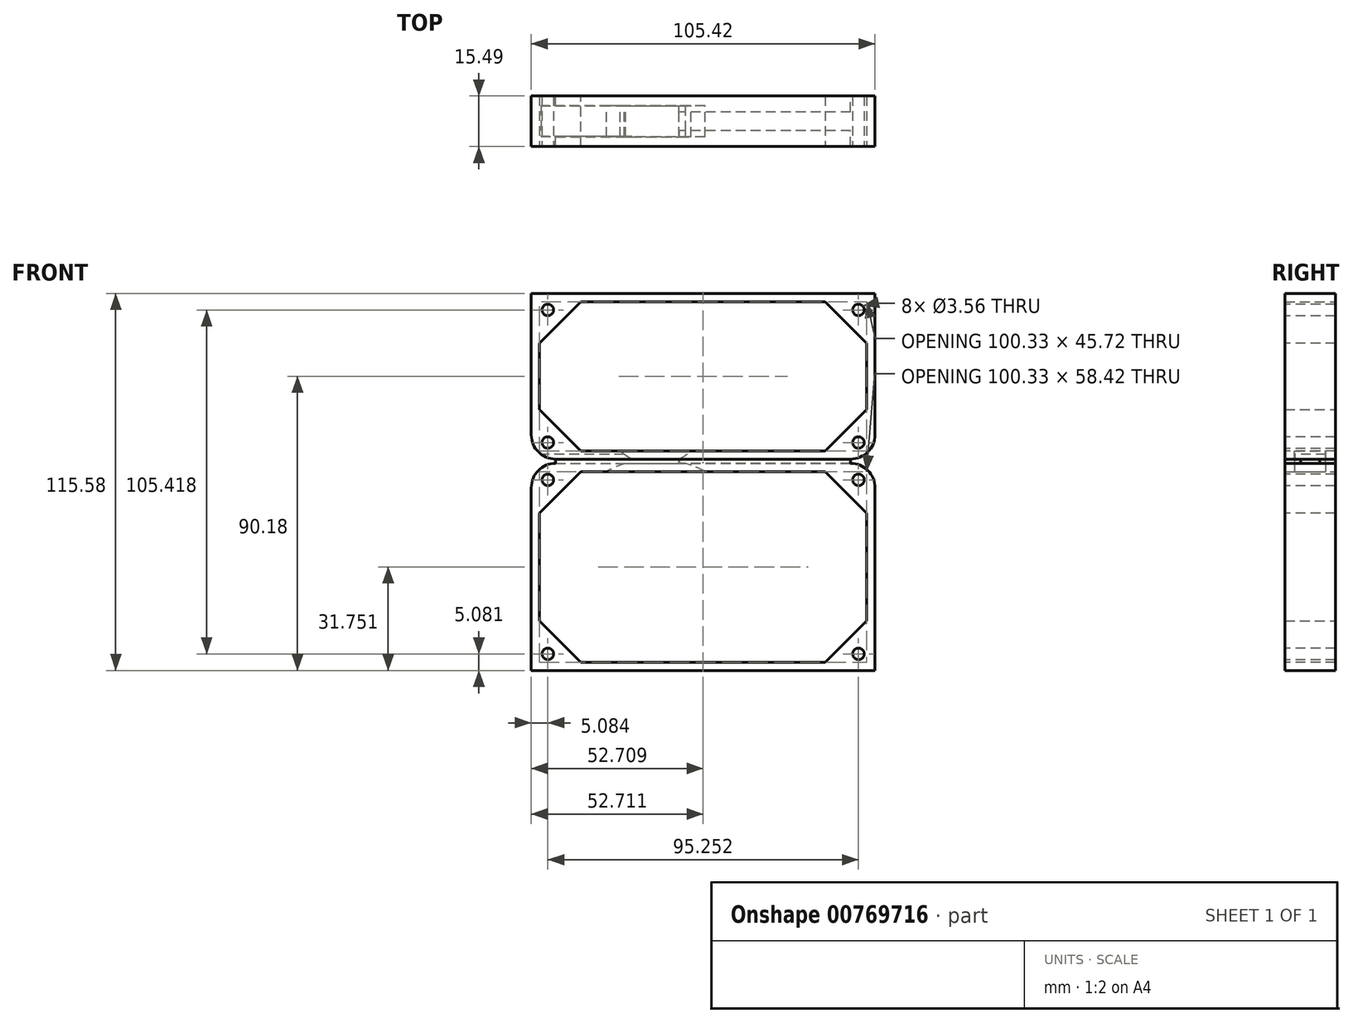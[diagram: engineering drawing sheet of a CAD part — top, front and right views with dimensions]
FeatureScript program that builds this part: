
annotation { "Feature Type Name" : "Feature", "Feature Type Description" : "" }
export const myFeature = defineFeature(function(context is Context, id is Id, definition is map)
    precondition{}
    {
        {
            var Q0;
            Q0=qCreatedBy(makeId("Front.planeOp"),FACE);
            var sketch = newSketch(context, id + "F0", { "sketchPlane" : qUnion([Q0])});
            skLineSegment(sketch, "E0.bottom", {"start": v(-52.7, 0.64) * mm, "end": v(52.7, 0.64) * mm});
            skLineSegment(sketch, "E0.top", {"start": v(-52.7, 51.44) * mm, "end": v(52.7, 51.44) * mm});
            skLineSegment(sketch, "E0.left", {"start": v(-52.7, 0.64) * mm, "end": v(-52.7, 51.44) * mm});
            skLineSegment(sketch, "E0.right", {"start": v(52.7, 0.64) * mm, "end": v(52.7, 51.44) * mm});
            skSolve(sketch);
        }
        {
            var Q0;
            Q0=qCreatedBy(makeId("Front.planeOp"),FACE);
            var sketch = newSketch(context, id + "F1", { "sketchPlane" : qUnion([Q0])});
            skLineSegment(sketch, "E1.bottom", {"start": v(-52.7, -0.64) * mm, "end": v(52.7, -0.64) * mm});
            skLineSegment(sketch, "E1.top", {"start": v(-52.7, -64.14) * mm, "end": v(52.7, -64.14) * mm});
            skLineSegment(sketch, "E1.left", {"start": v(-52.7, -0.64) * mm, "end": v(-52.7, -64.14) * mm});
            skLineSegment(sketch, "E1.right", {"start": v(52.7, -0.64) * mm, "end": v(52.7, -64.14) * mm});
            skSolve(sketch);
        }
        {
            var Q0;
            Q0=makeQuery(id+"F0.imprint","IMPRINT",FACE,{"disambiguationData":[TD([[makeQuery(id+"F0.imprint","IMPRINT",EDGE,{"derivedFrom":sQuery(id+"F0.wireOp",EDGE,"E0.bottom")}),1.0]])]});
            extrude(context, id + "F2", {"entities" : qUnion([Q0]), "depth" : 15.5 * mm, "offsetDistance" : 25.4 * mm});
        }
        {
            var Q0;
            Q0=makeQuery(id+"F1.imprint","IMPRINT",FACE,{"disambiguationData":[TD([[makeQuery(id+"F1.imprint","IMPRINT",EDGE,{"derivedFrom":sQuery(id+"F1.wireOp",EDGE,"E1.bottom")}),-1.0]])]});
            extrude(context, id + "F3", {"entities" : qUnion([Q0]), "depth" : 15.5 * mm, "offsetDistance" : 25.4 * mm});
        }
        {
            var Q0;
            Q0=makeQuery(id+"F2.opExtrude","CAP_FACE",FACE,{"disambiguationData":[OSD([sQuery(id+"F0.wireOp",EDGE,"E0.bottom"),sQuery(id+"F0.wireOp",EDGE,"E0.top"),sQuery(id+"F0.wireOp",EDGE,"E0.left"),sQuery(id+"F0.wireOp",EDGE,"E0.right")])],"isStart":false});
            var sketch = newSketch(context, id + "F4", { "sketchPlane" : qUnion([Q0])});
            skLineSegment(sketch, "E2.bottom", {"start": v(-50.17, 48.9) * mm, "end": v(50.16, 48.9) * mm});
            skLineSegment(sketch, "E2.top", {"start": v(-50.17, 3.18) * mm, "end": v(50.16, 3.18) * mm});
            skLineSegment(sketch, "E2.left", {"start": v(-50.17, 48.9) * mm, "end": v(-50.17, 3.18) * mm});
            skLineSegment(sketch, "E2.right", {"start": v(50.16, 48.9) * mm, "end": v(50.16, 3.18) * mm});
            skSolve(sketch);
        }
        {
            var Q0;
            Q0=makeQuery(id+"F3.opExtrude","CAP_FACE",FACE,{"disambiguationData":[OSD([sQuery(id+"F1.wireOp",EDGE,"E1.bottom"),sQuery(id+"F1.wireOp",EDGE,"E1.top"),sQuery(id+"F1.wireOp",EDGE,"E1.left"),sQuery(id+"F1.wireOp",EDGE,"E1.right")])],"isStart":false});
            var sketch = newSketch(context, id + "F5", { "sketchPlane" : qUnion([Q0])});
            skLineSegment(sketch, "E3.bottom", {"start": v(-50.16, -3.18) * mm, "end": v(50.17, -3.18) * mm});
            skLineSegment(sketch, "E3.top", {"start": v(-50.16, -61.6) * mm, "end": v(50.17, -61.6) * mm});
            skLineSegment(sketch, "E3.left", {"start": v(-50.16, -3.18) * mm, "end": v(-50.16, -61.6) * mm});
            skLineSegment(sketch, "E3.right", {"start": v(50.17, -3.18) * mm, "end": v(50.17, -61.6) * mm});
            skSolve(sketch);
        }
        {
            var Q0;
            Q0 = qSketchRegion(id + "F4", true);
            extrude(context, id + "F6", {"entities" : qUnion([Q0]), "operationType" : NewBodyOperationType.REMOVE, "oppositeDirection" : true, "depth" : 25.4 * mm, "offsetDistance" : 25.4 * mm});
        }
        {
            var Q0;
            Q0 = qSketchRegion(id + "F5", true);
            extrude(context, id + "F7", {"entities" : qUnion([Q0]), "operationType" : NewBodyOperationType.REMOVE, "oppositeDirection" : true, "depth" : 25.4 * mm, "offsetDistance" : 25.4 * mm});
        }
        {
            var Q0;
            Q0=makeQuery(id+"F6.boolean.opBoolean","COPY",EDGE,{"derivedFrom":makeQuery(id+"F6.opExtrude","SWEPT_EDGE",EDGE,{"disambiguationData":[OSD([sQuery(id+"F4.wireOp",EDGE,"E2.bottom"),sQuery(id+"F4.wireOp",EDGE,"E2.left")])]})});
            var Q1;
            Q1=makeQuery(id+"F6.boolean.opBoolean","COPY",EDGE,{"derivedFrom":makeQuery(id+"F6.opExtrude","SWEPT_EDGE",EDGE,{"disambiguationData":[OSD([sQuery(id+"F4.wireOp",EDGE,"E2.top"),sQuery(id+"F4.wireOp",EDGE,"E2.left")])]})});
            var Q2;
            Q2=makeQuery(id+"F6.boolean.opBoolean","COPY",EDGE,{"derivedFrom":makeQuery(id+"F6.opExtrude","SWEPT_EDGE",EDGE,{"disambiguationData":[OSD([sQuery(id+"F4.wireOp",EDGE,"E2.bottom"),sQuery(id+"F4.wireOp",EDGE,"E2.right")])]})});
            var Q3;
            Q3=makeQuery(id+"F6.boolean.opBoolean","COPY",EDGE,{"derivedFrom":makeQuery(id+"F6.opExtrude","SWEPT_EDGE",EDGE,{"disambiguationData":[OSD([sQuery(id+"F4.wireOp",EDGE,"E2.top"),sQuery(id+"F4.wireOp",EDGE,"E2.right")])]})});
            chamfer(context, id + "F8", {"entities" : qUnion([Q0, Q1, Q2, Q3]), "width" : 12.7 * mm, "tangentPropagation" : true});
        }
        {
            var Q0;
            Q0=makeQuery(id+"F7.boolean.opBoolean","COPY",EDGE,{"derivedFrom":makeQuery(id+"F7.opExtrude","SWEPT_EDGE",EDGE,{"disambiguationData":[OSD([sQuery(id+"F5.wireOp",EDGE,"E3.bottom"),sQuery(id+"F5.wireOp",EDGE,"E3.left")])]})});
            var Q1;
            Q1=makeQuery(id+"F7.boolean.opBoolean","COPY",EDGE,{"derivedFrom":makeQuery(id+"F7.opExtrude","SWEPT_EDGE",EDGE,{"disambiguationData":[OSD([sQuery(id+"F5.wireOp",EDGE,"E3.bottom"),sQuery(id+"F5.wireOp",EDGE,"E3.right")])]})});
            var Q2;
            Q2=makeQuery(id+"F7.boolean.opBoolean","COPY",EDGE,{"derivedFrom":makeQuery(id+"F7.opExtrude","SWEPT_EDGE",EDGE,{"disambiguationData":[OSD([sQuery(id+"F5.wireOp",EDGE,"E3.top"),sQuery(id+"F5.wireOp",EDGE,"E3.left")])]})});
            var Q3;
            Q3=makeQuery(id+"F7.boolean.opBoolean","COPY",EDGE,{"derivedFrom":makeQuery(id+"F7.opExtrude","SWEPT_EDGE",EDGE,{"disambiguationData":[OSD([sQuery(id+"F5.wireOp",EDGE,"E3.top"),sQuery(id+"F5.wireOp",EDGE,"E3.right")])]})});
            chamfer(context, id + "F9", {"entities" : qUnion([Q0, Q1, Q2, Q3]), "width" : 12.7 * mm, "tangentPropagation" : true});
        }
        {
            var Q0;
            Q0=makeQuery(id+"F2.opExtrude","CAP_FACE",FACE,{"disambiguationData":[OSD([sQuery(id+"F0.wireOp",EDGE,"E0.bottom"),sQuery(id+"F0.wireOp",EDGE,"E0.top"),sQuery(id+"F0.wireOp",EDGE,"E0.left"),sQuery(id+"F0.wireOp",EDGE,"E0.right")])],"isStart":false});
            var sketch = newSketch(context, id + "F10", { "sketchPlane" : qUnion([Q0])});
            skCircle(sketch, "E4", {"center": v(-47.63, 46.36) * mm, "radius": 1.78 * mm});
            skCircle(sketch, "E5", {"center": v(47.62, 46.36) * mm, "radius": 1.78 * mm});
            skCircle(sketch, "E6", {"center": v(47.62, 5.72) * mm, "radius": 1.78 * mm});
            skCircle(sketch, "E7", {"center": v(-47.63, 5.72) * mm, "radius": 1.78 * mm});
            skSolve(sketch);
        }
        {
            var Q0;
            Q0=makeQuery(id+"F3.opExtrude","CAP_FACE",FACE,{"disambiguationData":[OSD([sQuery(id+"F1.wireOp",EDGE,"E1.bottom"),sQuery(id+"F1.wireOp",EDGE,"E1.top"),sQuery(id+"F1.wireOp",EDGE,"E1.left"),sQuery(id+"F1.wireOp",EDGE,"E1.right")])],"isStart":false});
            var sketch = newSketch(context, id + "F11", { "sketchPlane" : qUnion([Q0])});
            skCircle(sketch, "E8", {"center": v(-47.62, -5.72) * mm, "radius": 1.78 * mm});
            skCircle(sketch, "E9", {"center": v(47.63, -5.72) * mm, "radius": 1.78 * mm});
            skCircle(sketch, "E10", {"center": v(47.63, -59.06) * mm, "radius": 1.78 * mm});
            skCircle(sketch, "E11", {"center": v(-47.62, -59.06) * mm, "radius": 1.78 * mm});
            skSolve(sketch);
        }
        {
            var Q0;
            Q0 = qSketchRegion(id + "F10", true);
            extrude(context, id + "F12", {"entities" : qUnion([Q0]), "operationType" : NewBodyOperationType.REMOVE, "oppositeDirection" : true, "depth" : 25.4 * mm, "offsetDistance" : 25.4 * mm});
        }
        {
            var Q0;
            Q0 = qSketchRegion(id + "F11", true);
            extrude(context, id + "F13", {"entities" : qUnion([Q0]), "operationType" : NewBodyOperationType.REMOVE, "oppositeDirection" : true, "depth" : 25.4 * mm, "offsetDistance" : 25.4 * mm});
        }
        {
            var Q0;
            Q0=qCreatedBy(makeId("Front.planeOp"),FACE);
            cPlane(context, id + "F14", {"entities" : qUnion([Q0]), "cplaneType" : CPlaneType.OFFSET, "offset" : 7.75 * mm, "width" : 152.4 * mm, "height" : 152.4 * mm});
        }
        {
            var Q0;
            Q0=qCreatedBy(id+"F14.planeOp",FACE);
            var sketch = newSketch(context, id + "F15", { "sketchPlane" : qUnion([Q0])});
            skCircle(sketch, "E12", {"center": v(-14.57, -30.13) * mm, "radius": 30.9 * mm});
            skCircle(sketch, "E13", {"center": v(-14.57, 14.76) * mm, "radius": 15.86 * mm});
            skSolve(sketch);
        }
        {
            var Q0;
            Q0 = qSketchRegion(id + "F15", true);
            extrude(context, id + "F16", {"entities" : qUnion([Q0]), "operationType" : NewBodyOperationType.REMOVE, "endBound" : BoundingType.SYMMETRIC, "depth" : 9.52 * mm, "offsetDistance" : 25.4 * mm});
        }
        {
            var Q0;
            Q0=makeQuery(id+"F2.opExtrude","SWEPT_EDGE",EDGE,{"disambiguationData":[OSD([sQuery(id+"F0.wireOp",EDGE,"E0.bottom"),sQuery(id+"F0.wireOp",EDGE,"E0.right")])]});
            var Q1;
            Q1=makeQuery(id+"F3.opExtrude","SWEPT_EDGE",EDGE,{"disambiguationData":[OSD([sQuery(id+"F1.wireOp",EDGE,"E1.bottom"),sQuery(id+"F1.wireOp",EDGE,"E1.right")])]});
            var Q2;
            Q2=makeQuery(id+"F2.opExtrude","SWEPT_EDGE",EDGE,{"disambiguationData":[OSD([sQuery(id+"F0.wireOp",EDGE,"E0.bottom"),sQuery(id+"F0.wireOp",EDGE,"E0.left")])]});
            var Q3;
            Q3=makeQuery(id+"F3.opExtrude","SWEPT_EDGE",EDGE,{"disambiguationData":[OSD([sQuery(id+"F1.wireOp",EDGE,"E1.bottom"),sQuery(id+"F1.wireOp",EDGE,"E1.left")])]});
            fillet(context, id + "F17", {"entities" : qUnion([Q0, Q1, Q2, Q3]), "radius" : 7.48 * mm, "tangentPropagation" : true, "allowEdgeOverflow" : false});
        }
        {
            var Q0;
            Q0=makeQuery(id+"F3.opExtrude","SWEPT_FACE",FACE,{"disambiguationData":[OSD([sQuery(id+"F1.wireOp",EDGE,"E1.bottom")])]});
            var sketch = newSketch(context, id + "F18", { "sketchPlane" : qUnion([Q0])});
            skLineSegment(sketch, "E14.bottom", {"start": v(45.23, -15.5) * mm, "end": v(-7.33, -15.5) * mm});
            skLineSegment(sketch, "E14.top", {"start": v(45.23, -10.63) * mm, "end": v(-7.33, -10.63) * mm});
            skLineSegment(sketch, "E14.left", {"start": v(45.23, -15.5) * mm, "end": v(45.23, -10.63) * mm});
            skLineSegment(sketch, "E14.right", {"start": v(-7.33, -15.5) * mm, "end": v(-7.33, -10.63) * mm});
            skPoint(sketch, "E15.oppositeSnap0", {"position": v(-7.33, -13.06) * mm});
            skLineSegment(sketch, "E15.bottom", {"start": v(-45.22, -15.5) * mm, "end": v(-7.33, -15.5) * mm});
            skLineSegment(sketch, "E15.top", {"start": v(-45.22, -12.5) * mm, "end": v(-7.33, -12.5) * mm});
            skLineSegment(sketch, "E15.left", {"start": v(-45.22, -15.5) * mm, "end": v(-45.22, -12.5) * mm});
            skLineSegment(sketch, "E15.right", {"start": v(-7.33, -15.5) * mm, "end": v(-7.33, -12.5) * mm});
            skSolve(sketch);
        }
        {
            var Q0;
            Q0 = qSketchRegion(id + "F18", true);
            extrude(context, id + "F19", {"entities" : qUnion([Q0]), "operationType" : NewBodyOperationType.ADD, "depth" : 1.27 * mm, "offsetDistance" : 25.4 * mm});
        }
        {
            var Q0;
            Q0=makeQuery(id+"F2.opExtrude","SWEPT_FACE",FACE,{"disambiguationData":[OSD([sQuery(id+"F0.wireOp",EDGE,"E0.bottom")])]});
            var sketch = newSketch(context, id + "F20", { "sketchPlane" : qUnion([Q0])});
            skLineSegment(sketch, "E16.bottom", {"start": v(45.22, 0) * mm, "end": v(-7.35, 0) * mm});
            skLineSegment(sketch, "E16.top", {"start": v(45.22, 4.86) * mm, "end": v(-7.35, 4.86) * mm});
            skLineSegment(sketch, "E16.left", {"start": v(45.22, 0) * mm, "end": v(45.22, 4.86) * mm});
            skLineSegment(sketch, "E16.right", {"start": v(-7.35, 0) * mm, "end": v(-7.35, 4.86) * mm});
            skLineSegment(sketch, "E17.bottom", {"start": v(-45.22, 0) * mm, "end": v(-7.35, 0) * mm});
            skLineSegment(sketch, "E17.top", {"start": v(-45.22, 2.98) * mm, "end": v(-7.35, 2.98) * mm});
            skLineSegment(sketch, "E17.left", {"start": v(-45.22, 0) * mm, "end": v(-45.22, 2.98) * mm});
            skLineSegment(sketch, "E17.right", {"start": v(-7.35, 0) * mm, "end": v(-7.35, 2.98) * mm});
            skSolve(sketch);
        }
        {
            var Q0;
            Q0 = qSketchRegion(id + "F20", true);
            extrude(context, id + "F21", {"entities" : qUnion([Q0]), "operationType" : NewBodyOperationType.ADD, "depth" : 1.27 * mm, "offsetDistance" : 25.4 * mm});
        }
        {
            var Q0;
            Q0=makeQuery(id+"F2.opExtrude","SWEPT_FACE",FACE,{"disambiguationData":[OSD([sQuery(id+"F0.wireOp",EDGE,"E0.bottom")])]});
            var sketch = newSketch(context, id + "F22", { "sketchPlane" : qUnion([Q0])});
            skLineSegment(sketch, "E18.bottom", {"start": v(-21.79, 2.98) * mm, "end": v(-55.25, 2.98) * mm});
            skLineSegment(sketch, "E18.top", {"start": v(-21.79, 12.45) * mm, "end": v(-55.25, 12.45) * mm});
            skLineSegment(sketch, "E18.left", {"start": v(-21.79, 2.98) * mm, "end": v(-21.79, 12.45) * mm});
            skLineSegment(sketch, "E18.right", {"start": v(-55.25, 2.98) * mm, "end": v(-55.25, 12.45) * mm});
            skSolve(sketch);
        }
        {
            var Q0;
            Q0 = qSketchRegion(id + "F22", true);
            extrude(context, id + "F23", {"entities" : qUnion([Q0]), "operationType" : NewBodyOperationType.REMOVE, "oppositeDirection" : true, "depth" : 1.52 * mm, "offsetDistance" : 25.4 * mm});
        }
    });
